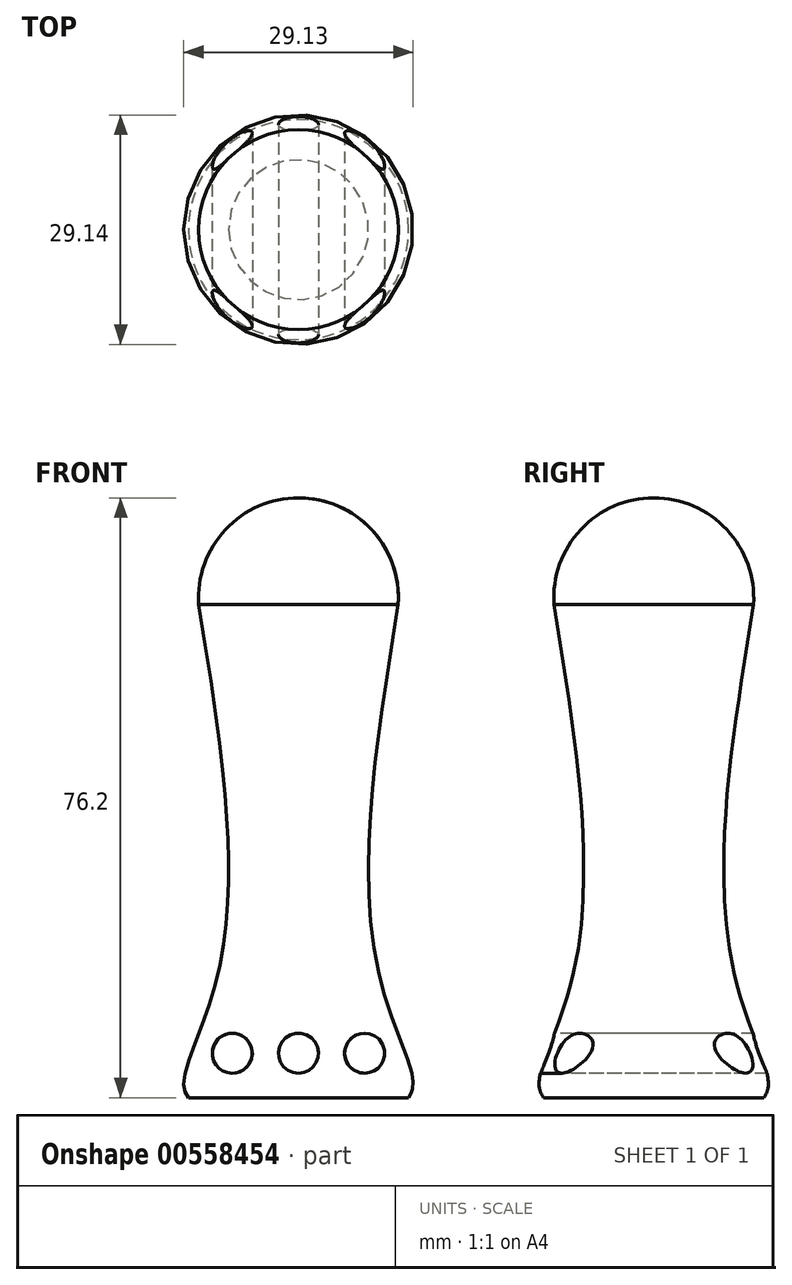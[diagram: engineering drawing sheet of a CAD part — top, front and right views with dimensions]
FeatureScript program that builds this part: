
annotation { "Feature Type Name" : "Feature", "Feature Type Description" : "" }
export const myFeature = defineFeature(function(context is Context, id is Id, definition is map)
    precondition{}
    {
        {
            var Q0;
            Q0=qCreatedBy(makeId("Front.planeOp"),FACE);
            var sketch = newSketch(context, id + "F0", { "sketchPlane" : qUnion([Q0])});
            skLineSegment(sketch, "E0", {"start": v(0, 0) * mm, "end": v(0, 63.5) * mm});
            skArc(sketch, "E1", {"start": v(12.67, 62.65) * mm, "mid": v(9.27, 72.18) * mm, "end": v(0, 76.2) * mm});
            skFitSpline(sketch, "E2", {"points": [v(12.67, 62.65) * mm, v(8.9, 30.4) * mm, v(10.86, 13.28) * mm, v(14.57, 1.96) * mm, v(13.98, 0) * mm], "startDerivative": vector(-20.4, -125.01) * mm, "endDerivative": vector(-9.89, -14.94) * mm});
            skLineSegment(sketch, "E3", {"start": v(0, 0) * mm, "end": v(13.98, 0) * mm});
            skLineSegment(sketch, "E4", {"start": v(0, 63.5) * mm, "end": v(0, 76.2) * mm});
            skSolve(sketch);
        }
        {
            var Q0;
            Q0=makeQuery(id+"F0.imprint","IMPRINT",FACE,{"disambiguationData":[TD([[makeQuery(id+"F0.imprint","IMPRINT",EDGE,{"derivedFrom":sQuery(id+"F0.wireOp",EDGE,"E0")}),-1.0]])]});
            var Q1;
            Q1=sQuery(id+"F0.wireOp",EDGE,"E0");
            revolve(context, id + "F1", {"entities" : qUnion([Q0]), "axis" : qUnion([Q1]), "revolveType" : RevolveType.FULL});
        }
        {
            var Q0;
            Q0=qCreatedBy(makeId("Front.planeOp"),FACE);
            var sketch = newSketch(context, id + "F2", { "sketchPlane" : qUnion([Q0])});
            skCircle(sketch, "E5", {"center": v(0, 5.64) * mm, "radius": 2.54 * mm});
            skCircle(sketch, "E6", {"center": v(8.4, 5.64) * mm, "radius": 2.54 * mm});
            skCircle(sketch, "E7.MirrorC", {"center": v(-8.4, 5.64) * mm, "radius": 2.54 * mm});
            skSolve(sketch);
        }
        {
            var Q0;
            Q0 = qSketchRegion(id + "F2", true);
            extrude(context, id + "F3", {"entities" : qUnion([Q0]), "operationType" : NewBodyOperationType.REMOVE, "endBound" : BoundingType.SYMMETRIC, "oppositeDirection" : true, "depth" : 71.12 * mm, "offsetDistance" : 25.4 * mm});
        }
    });
